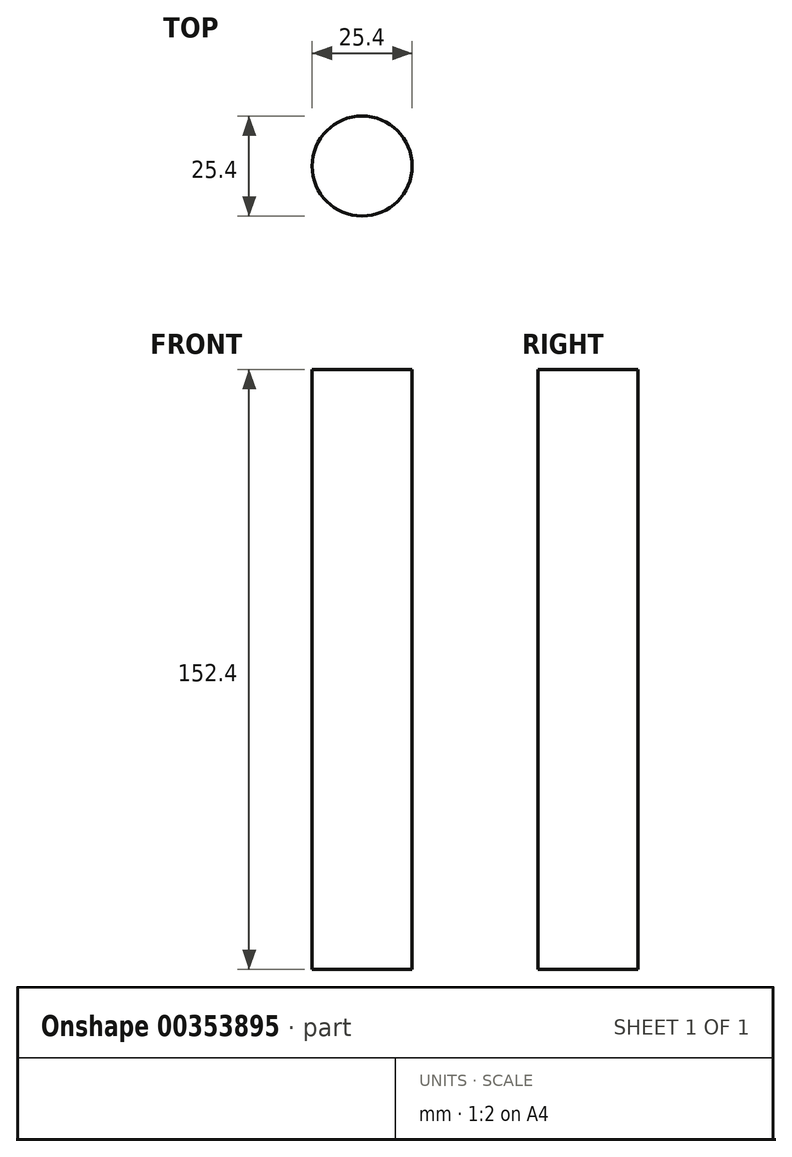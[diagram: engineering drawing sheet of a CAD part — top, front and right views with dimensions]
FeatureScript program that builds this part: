
annotation { "Feature Type Name" : "Feature", "Feature Type Description" : "" }
export const myFeature = defineFeature(function(context is Context, id is Id, definition is map)
    precondition{}
    {
        {
            var Q0;
            Q0=qCreatedBy(makeId("Top.planeOp"),FACE);
            var sketch = newSketch(context, id + "F0", { "sketchPlane" : qUnion([Q0])});
            skCircle(sketch, "E0", {"center": v(0, 0) * mm, "radius": 12.7 * mm});
            skSolve(sketch);
        }
        {
            var Q0;
            Q0=makeQuery(id+"F0.imprint","IMPRINT",FACE,{"disambiguationData":[TD([[makeQuery(id+"F0.imprint","IMPRINT",EDGE,{"derivedFrom":sQuery(id+"F0.wireOp",EDGE,"E0")}),1.0]])]});
            extrude(context, id + "F1", {"entities" : qUnion([Q0]), "endBound" : BoundingType.SYMMETRIC, "depth" : 152.4 * mm});
        }
    });
